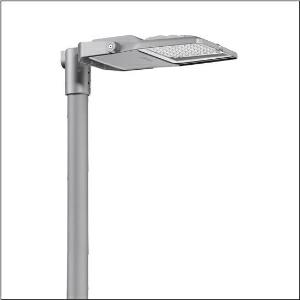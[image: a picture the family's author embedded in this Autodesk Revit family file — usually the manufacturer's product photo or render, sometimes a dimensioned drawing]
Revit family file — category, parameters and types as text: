
# Revit family: floodlight_fl_21_mini___pl43_5xa7776c2a3a_c8bd
name_source: partatom
category: Lighting Fixtures
units: mm (PartAtom-declared; Revit-internal decimal feet)

## family parameters
Cut with Voids When Loaded = No
Host = Face
Light Source = No
Part Type = Normal
Room Calculation Point = No
Round Connector Dimension = Use Diameter
Shared = No

## types (1)
- --- (1 x LED, 12500 lm, 89 W, 3000K)
    Apparent Load = 89 VA
    CIE Flux Codes = 27 78 99 100 100
    Color Rendering = 70
    Color Temperature = 3000K
    Default Elevation = 1800 mm
    Description = Floodlight FL 21 mini, floodlight, primary light control with lens, of PMMA, primary optical cover: protective disc, of toughened safety glass, transparent, light distribution: PL43, light emission: direct distribution, installation type: surface-mounted, LED, High Power LED, rated luminous flux: 12.500lm, luminous efficacy: 140lm/W, light colour: 730, colour temperature: 3000K, control: flexible luminous flux parameterisation, time-dependent luminous flux control, constant luminous flux control, overheat protection, presetting dimming logarithmic, with terminal, 6-pole, mains connection: 220..240V, AC, 50/60Hz, start of lifetime: 89W, end of service life: 94W, reduction: 43W, luminaire housing, of diecast aluminium, powder-coated, Siteco® metallic grey (DB 702S), corrosivity category C5 mid according to DIN EN ISO 12944, sealing non-destructively replaceable, please order mast flange separately, mast bracket, of steel, galvanised, powder-coated, Siteco® metallic grey (DB 702S), Smart Interface below and above, protection rating (complete): IP66, insulation class (complete): insulation class II (safety insulation), certification: CE, ENEC, VDE, protection symbol: D, impact resistance: IK08, permissible operating ambient temperature: -40..+40°C, permissible operating ambient temperature for outdoor applications: -40..+50°C, standard: DIN EN 12944, LABS conformity tested according to VDMA 24364:2018-05, packaging unit: 1 piece

Light Distribution: PL43
    Height = 70 mm
    Lamp = 1 x LED
    Lamp Light Flux = 12500 lm
    Lamp Power = 89 W
    Lamp count = 1
    Length = 485 mm
    Luminous efficacy = 140 lm/W
    Manufacturer = Siteco
    ModVariant = No
    Model = 5XA7776C2A3A
    Number of Poles = 1
    OnlyDefault = Yes
    Power Factor = 1
    Product Name = Floodlight FL 21 mini | PL43
    Product group = floodlight | pylon annexe
    ProductGroupID = 6200
    Protection Class = Protection class II
    Protection Degree = IP 66
    RLX_Detail_Level = 1
    RLX_Emergency_Light_Flux = 0 lm
    RLX_Emergency_Type = 0
    RLX_Emergency_Type_DB = No
    RlxData = <blob elided: 100741 chars, md5=d89ec759>
    Socket = socket
    Standby Power = 0 W
    System Light Flux = 12500 lm
    System Power = 89 W
    Type Comments = factory setting: luminous flux: 100 % | dim-lin: 254 | 456 mA
    Type Image = l_1007125.jpg
    URL = http://relux.com
    VarID = @adj_093395
    Voltage = 0 V
    Weight = 0.00 kg
    Width = 337 mm

## geometry (parser evidence)
native form markers: Blend x4, Sweep x11
no freeform markers — native parametric forms only
